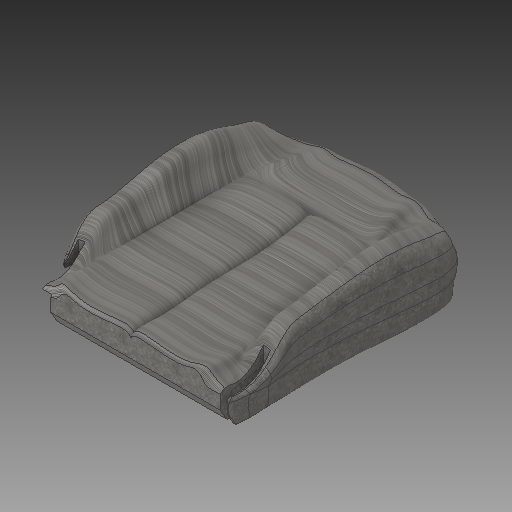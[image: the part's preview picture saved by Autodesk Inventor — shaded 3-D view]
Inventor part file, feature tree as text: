
AUTODESK INVENTOR PART (.ipt)
format: ipt  version: 2019 (Build 230136000, 136)  size: 2,259,456 bytes
history: native  units: in
note: dims shown in document units (in); Inventor stores cm internally (conversion verified against a paired STEP export)
features: sketch x14, other x12, plane x5
ambient origin geometry x8: Origin, YZ Plane, XZ Plane, XY Plane, X Axis, Y Axis, Z Axis, Center Point
bodies: Solid1 (feature_tree)
feature tree (31):
  other  "Lower Seat Cushion.ipt"
  other  "Blocks"
  other  "Block1"
  other  "Block2"
  other  "Block3"
  other  "Block4"
  other  "Block5"
  other  "Block6"
  other  "Solid1::Lower Seat Cushion.ipt"
  other  "TaggingFeature1"
  sketch  "Sketch1"  dims[d0=0.3937in]
  sketch  "Sketch2"
  sketch  "Sketch3"
  sketch  "Sketch4"
  sketch  "Sketch5"
  sketch  "Sketch8"
  sketch  "Sketch9"
  sketch  "Sketch10"
  sketch  "Sketch12"
  sketch  "Sketch13"
  sketch  "Sketch14"
  sketch  "Sketch15"
  sketch  "Sketch16"
  sketch  "Sketch17"
  plane  "Work Plane1"
  plane  "Work Plane2"
  plane  "Work Plane3"
  plane  "Work Plane4"
  plane  "Work Plane5"
  other  "Block2:1"
  other  "Block3:1"
